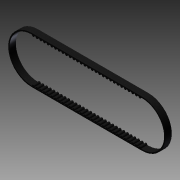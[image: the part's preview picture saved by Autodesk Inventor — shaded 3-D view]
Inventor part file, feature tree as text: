
AUTODESK INVENTOR PART (.ipt)
format: ipt  version: 2012 (Build 160160000, 160)  size: 400,896 bytes
history: native  units: in
note: dims shown in document units (in); Inventor stores cm internally (conversion verified against a paired STEP export)
features: extrude x1, sketch x1
ambient origin geometry x8: Origin, YZ Plane, XZ Plane, XY Plane, X Axis, Y Axis, Z Axis, Center Point
bodies: Solid1 (feature_tree)
feature tree (2):
  extrude  "Extrusion1"  Depth=1.231in
  sketch  "Sketch1"  dims[d0=6.125in d1=1.231in d2=1.3in d4=0.0625in d5=0.024in d6=0.01in d7=11.811in d9=0.204in d10=0.3937in d12=1.0in d14=0.3543in d15=0.0in d16=1.231in]
